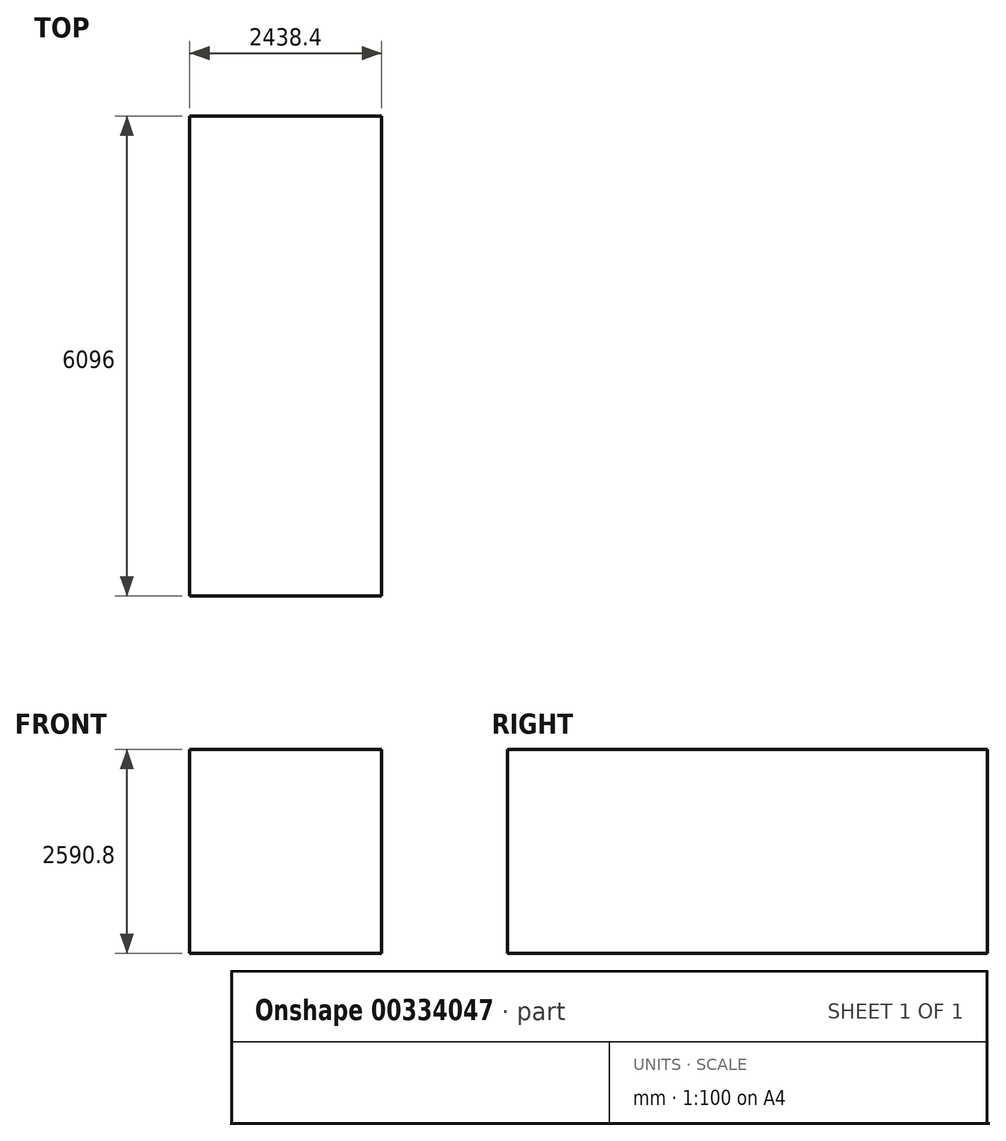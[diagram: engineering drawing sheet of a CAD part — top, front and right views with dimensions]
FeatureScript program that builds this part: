
annotation { "Feature Type Name" : "Feature", "Feature Type Description" : "" }
export const myFeature = defineFeature(function(context is Context, id is Id, definition is map)
    precondition{}
    {
        {
            var Q0;
            Q0=qCreatedBy(makeId("Front.planeOp"),FACE);
            var sketch = newSketch(context, id + "F0", { "sketchPlane" : qUnion([Q0])});
            skLineSegment(sketch, "E0.bottom", {"start": v(-1219.2, 1295.4) * mm, "end": v(1219.2, 1295.4) * mm});
            skLineSegment(sketch, "E0.top", {"start": v(-1219.2, -1295.4) * mm, "end": v(1219.2, -1295.4) * mm});
            skLineSegment(sketch, "E0.left", {"start": v(-1219.2, 1295.4) * mm, "end": v(-1219.2, -1295.4) * mm});
            skLineSegment(sketch, "E0.right", {"start": v(1219.2, 1295.4) * mm, "end": v(1219.2, -1295.4) * mm});
            skLineSegment(sketch, "E1", {"start": v(-562.56, 635.46) * mm, "end": v(-562.56, -1193.34) * mm});
            skLineSegment(sketch, "E2", {"start": v(0, 1295.4) * mm, "end": v(0, -1295.4) * mm, "construction": true});
            skLineSegment(sketch, "E3", {"start": v(-1219.2, 0) * mm, "end": v(1219.2, 0) * mm, "construction": true});
            skLineSegment(sketch, "E4", {"start": v(-562.56, -1193.34) * mm, "end": v(0, -1193.34) * mm});
            skLineSegment(sketch, "E5", {"start": v(-562.56, 635.46) * mm, "end": v(0, 635.46) * mm});
            skLineSegment(sketch, "E6.MirrorCS", {"start": v(562.56, 635.46) * mm, "end": v(0, 635.46) * mm});
            skLineSegment(sketch, "E7.MirrorCS", {"start": v(562.56, 635.46) * mm, "end": v(562.56, -1193.34) * mm});
            skLineSegment(sketch, "E8.MirrorCS", {"start": v(562.56, -1193.34) * mm, "end": v(0, -1193.34) * mm});
            skSolve(sketch);
        }
        {
            var Q0;
            Q0=makeQuery(id+"F0.imprint","IMPRINT",FACE,{"disambiguationData":[TD([[makeQuery(id+"F0.imprint","IMPRINT",EDGE,{"derivedFrom":sQuery(id+"F0.wireOp",EDGE,"E0.bottom")}),-1.0]])]});
            var Q1;
            Q1=makeQuery(id+"F0.imprint","IMPRINT",FACE,{"disambiguationData":[TD([[makeQuery(id+"F0.imprint","IMPRINT",EDGE,{"derivedFrom":sQuery(id+"F0.wireOp",EDGE,"E1")}),1.0]])]});
            extrude(context, id + "F1", {"entities" : qUnion([Q0, Q1]), "depth" : 6096 * mm});
        }
    });
